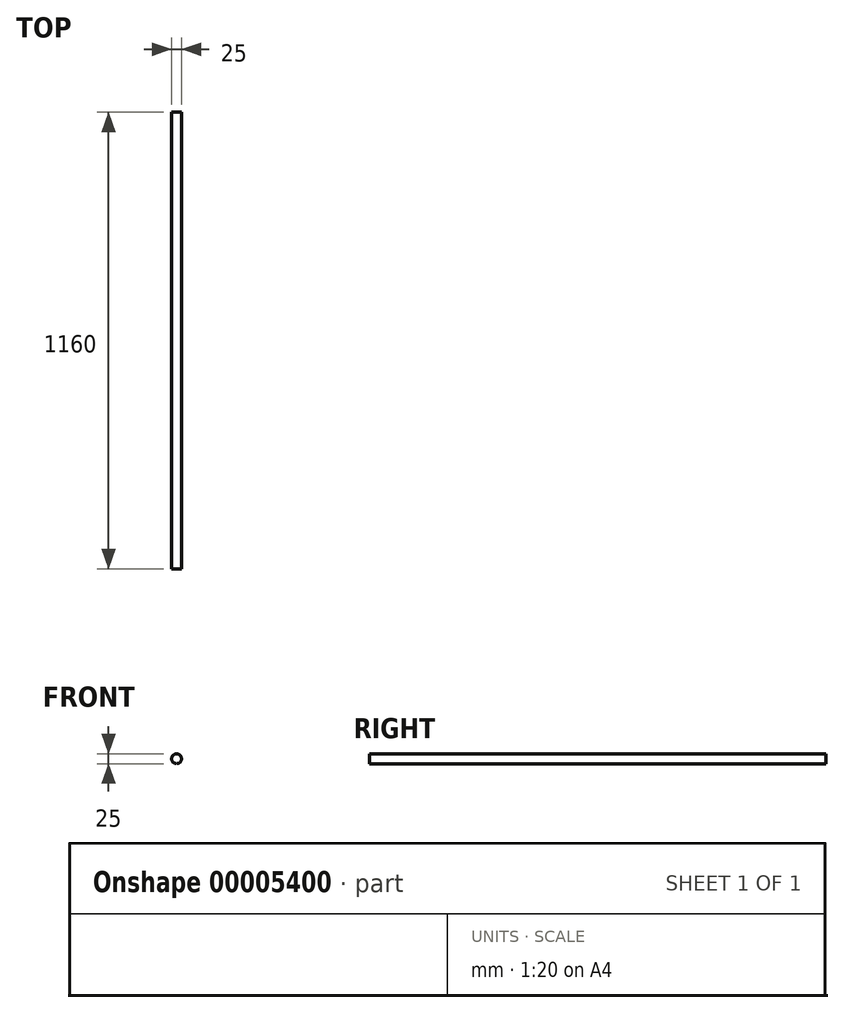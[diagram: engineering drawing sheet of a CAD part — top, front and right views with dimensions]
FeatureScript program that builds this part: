
annotation { "Feature Type Name" : "Feature", "Feature Type Description" : "" }
export const myFeature = defineFeature(function(context is Context, id is Id, definition is map)
    precondition{}
    {
        {
            var Q0;
            Q0=qCreatedBy(makeId("Front.planeOp"),FACE);
            var sketch = newSketch(context, id + "F0", { "sketchPlane" : qUnion([Q0])});
            skCircle(sketch, "E0", {"center": v(-38.52, 29) * mm, "radius": 12.5 * mm});
            skSolve(sketch);
        }
        {
            var Q0;
            Q0=makeQuery(id+"F0.imprint","IMPRINT",FACE,{"disambiguationData":[TD([[makeQuery(id+"F0.imprint","IMPRINT",EDGE,{"derivedFrom":sQuery(id+"F0.wireOp",EDGE,"E0")}),1.0]])]});
            extrude(context, id + "F1", {"entities" : qUnion([Q0]), "depth" : 1160 * mm});
        }
    });
